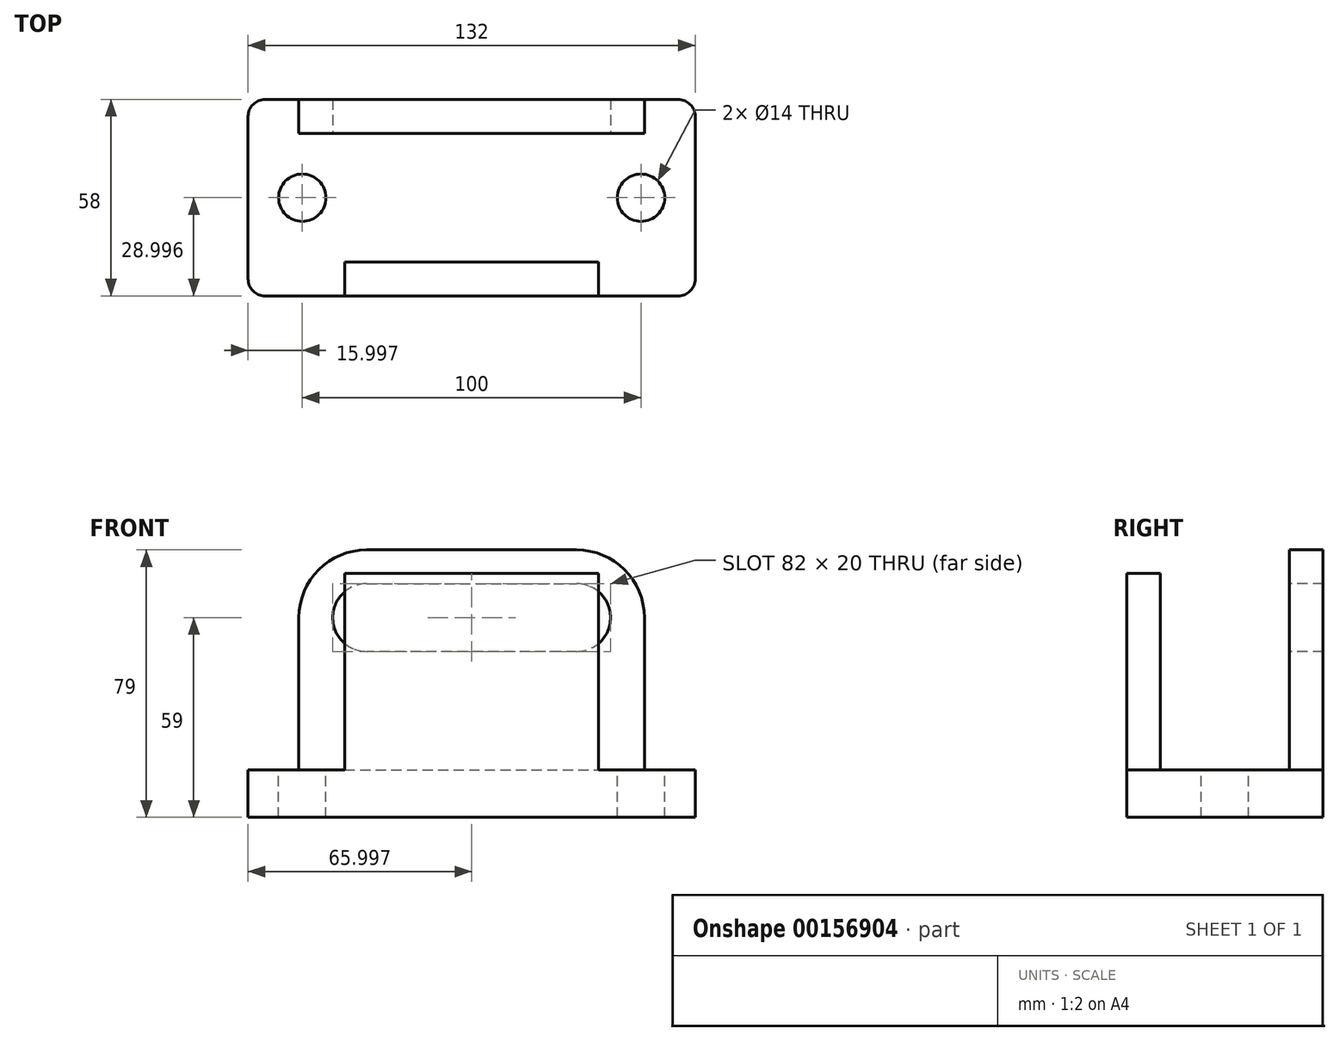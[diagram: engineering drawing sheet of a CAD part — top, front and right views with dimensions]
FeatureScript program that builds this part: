
annotation { "Feature Type Name" : "Feature", "Feature Type Description" : "" }
export const myFeature = defineFeature(function(context is Context, id is Id, definition is map)
    precondition{}
    {
        {
            var Q0;
            Q0=qCreatedBy(makeId("Top.planeOp"),FACE);
            var sketch = newSketch(context, id + "F0", { "sketchPlane" : qUnion([Q0])});
            skLineSegment(sketch, "E0.bottom", {"start": v(-73.57, -37.7) * mm, "end": v(48.43, -37.7) * mm});
            skLineSegment(sketch, "E0.top", {"start": v(-73.57, 20.3) * mm, "end": v(48.43, 20.3) * mm});
            skLineSegment(sketch, "E0.left", {"start": v(-78.57, -32.7) * mm, "end": v(-78.57, 15.3) * mm});
            skLineSegment(sketch, "E0.right", {"start": v(53.43, -32.7) * mm, "end": v(53.43, 15.3) * mm});
            skPoint(sketch, "E1.visualSharp", {"position": v(-78.57, -37.7) * mm});
            skArc(sketch, "E1.filletArc", {"start": v(-78.57, -32.7) * mm, "mid": v(-77.1, -36.24) * mm, "end": v(-73.57, -37.7) * mm});
            skPoint(sketch, "E2.visualSharp", {"position": v(53.43, -37.7) * mm});
            skArc(sketch, "E2.filletArc", {"start": v(48.43, -37.7) * mm, "mid": v(51.96, -36.24) * mm, "end": v(53.43, -32.7) * mm});
            skPoint(sketch, "E3.visualSharp", {"position": v(53.43, 20.3) * mm});
            skArc(sketch, "E3.filletArc", {"start": v(53.43, 15.3) * mm, "mid": v(51.96, 18.83) * mm, "end": v(48.43, 20.3) * mm});
            skPoint(sketch, "E4.visualSharp", {"position": v(-78.57, 20.3) * mm});
            skArc(sketch, "E4.filletArc", {"start": v(-73.57, 20.3) * mm, "mid": v(-77.1, 18.83) * mm, "end": v(-78.57, 15.3) * mm});
            skSolve(sketch);
        }
        {
            var Q0;
            Q0=makeQuery(id+"F0.imprint","IMPRINT",FACE,{"disambiguationData":[TD([[makeQuery(id+"F0.imprint","IMPRINT",EDGE,{"derivedFrom":sQuery(id+"F0.wireOp",EDGE,"E0.bottom")}),1.0]])]});
            extrude(context, id + "F1", {"entities" : qUnion([Q0]), "depth" : 14 * mm});
        }
        {
            var Q0;
            Q0=makeQuery(id+"F1.opExtrude","CAP_FACE",FACE,{"disambiguationData":[OSD([sQuery(id+"F0.wireOp",EDGE,"E0.bottom"),sQuery(id+"F0.wireOp",EDGE,"E0.top"),sQuery(id+"F0.wireOp",EDGE,"E0.left"),sQuery(id+"F0.wireOp",EDGE,"E0.right"),sQuery(id+"F0.wireOp",EDGE,"E1.filletArc"),sQuery(id+"F0.wireOp",EDGE,"E2.filletArc"),sQuery(id+"F0.wireOp",EDGE,"E3.filletArc"),sQuery(id+"F0.wireOp",EDGE,"E4.filletArc")])],"isStart":false});
            var sketch = newSketch(context, id + "F2", { "sketchPlane" : qUnion([Q0])});
            skLineSegment(sketch, "E5", {"start": v(-78.57, 15.3) * mm, "end": v(-78.57, 20.3) * mm});
            skLineSegment(sketch, "E6", {"start": v(-78.57, 20.3) * mm, "end": v(-63.57, 20.3) * mm});
            skLineSegment(sketch, "E7", {"start": v(-63.57, 20.3) * mm, "end": v(-63.57, 10.3) * mm});
            skLineSegment(sketch, "E8", {"start": v(-63.57, 10.3) * mm, "end": v(38.43, 10.3) * mm});
            skLineSegment(sketch, "E9", {"start": v(38.43, 10.3) * mm, "end": v(38.43, 20.3) * mm});
            skLineSegment(sketch, "E10", {"start": v(38.43, 20.3) * mm, "end": v(-63.57, 20.3) * mm});
            skSolve(sketch);
        }
        {
            var Q0;
            Q0=makeQuery(id+"F2.imprint","IMPRINT",FACE,{"disambiguationData":[TD([[makeQuery(id+"F2.imprint","IMPRINT",EDGE,{"derivedFrom":sQuery(id+"F2.wireOp",EDGE,"E7")}),1.0]])]});
            extrude(context, id + "F3", {"entities" : qUnion([Q0]), "operationType" : NewBodyOperationType.ADD, "depth" : 65 * mm});
        }
        {
            var Q0;
            Q0=makeQuery(id+"F3.opExtrude","CAP_EDGE",EDGE,{"disambiguationData":[OSD([sQuery(id+"F2.wireOp",EDGE,"E7")])],"isStart":false});
            var Q1;
            Q1=makeQuery(id+"F3.opExtrude","CAP_EDGE",EDGE,{"disambiguationData":[OSD([sQuery(id+"F2.wireOp",EDGE,"E9")])],"isStart":false});
            fillet(context, id + "F4", {"entities" : qUnion([Q0, Q1]), "radius" : 20 * mm, "tangentPropagation" : true, "allowEdgeOverflow" : false});
        }
        {
            var Q0;
            Q0=makeQuery(id+"F3.opExtrude","SWEPT_FACE",FACE,{"disambiguationData":[OSD([sQuery(id+"F2.wireOp",EDGE,"E8")])]});
            var sketch = newSketch(context, id + "F5", { "sketchPlane" : qUnion([Q0])});
            skLineSegment(sketch, "E11", {"start": v(-43.57, 69) * mm, "end": v(18.43, 69) * mm});
            skLineSegment(sketch, "E12", {"start": v(18.43, 49) * mm, "end": v(-43.57, 49) * mm});
            skArc(sketch, "E13", {"start": v(-43.57, 69) * mm, "mid": v(-53.57, 59) * mm, "end": v(-43.57, 49) * mm});
            skArc(sketch, "E14", {"start": v(18.43, 69) * mm, "mid": v(28.43, 59) * mm, "end": v(18.43, 49) * mm});
            skSolve(sketch);
        }
        {
            var Q0;
            Q0 = qSketchRegion(id + "F5", true);
            extrude(context, id + "F6", {"entities" : qUnion([Q0]), "operationType" : NewBodyOperationType.REMOVE, "oppositeDirection" : true, "depth" : 10 * mm});
        }
        {
            var Q0;
            Q0=makeQuery(id+"F1.opExtrude","CAP_FACE",FACE,{"disambiguationData":[OSD([sQuery(id+"F0.wireOp",EDGE,"E0.bottom"),sQuery(id+"F0.wireOp",EDGE,"E0.top"),sQuery(id+"F0.wireOp",EDGE,"E0.left"),sQuery(id+"F0.wireOp",EDGE,"E0.right"),sQuery(id+"F0.wireOp",EDGE,"E1.filletArc"),sQuery(id+"F0.wireOp",EDGE,"E2.filletArc"),sQuery(id+"F0.wireOp",EDGE,"E3.filletArc"),sQuery(id+"F0.wireOp",EDGE,"E4.filletArc")])],"isStart":false});
            var sketch = newSketch(context, id + "F7", { "sketchPlane" : qUnion([Q0])});
            skCircle(sketch, "E15", {"center": v(-62.57, -8.7) * mm, "radius": 7 * mm});
            skCircle(sketch, "E16", {"center": v(37.43, -8.7) * mm, "radius": 7 * mm});
            skSolve(sketch);
        }
        {
            var Q0;
            Q0=makeQuery(id+"F7.imprint","IMPRINT",FACE,{"disambiguationData":[TD([[makeQuery(id+"F7.imprint","IMPRINT",EDGE,{"derivedFrom":sQuery(id+"F7.wireOp",EDGE,"E15")}),1.0]])]});
            extrude(context, id + "F8", {"entities" : qUnion([Q0]), "operationType" : NewBodyOperationType.REMOVE, "oppositeDirection" : true, "depth" : 14 * mm});
        }
        {
            var Q0;
            Q0=makeQuery(id+"F1.opExtrude","CAP_FACE",FACE,{"disambiguationData":[OSD([sQuery(id+"F0.wireOp",EDGE,"E0.bottom"),sQuery(id+"F0.wireOp",EDGE,"E0.top"),sQuery(id+"F0.wireOp",EDGE,"E0.left"),sQuery(id+"F0.wireOp",EDGE,"E0.right"),sQuery(id+"F0.wireOp",EDGE,"E1.filletArc"),sQuery(id+"F0.wireOp",EDGE,"E2.filletArc"),sQuery(id+"F0.wireOp",EDGE,"E3.filletArc"),sQuery(id+"F0.wireOp",EDGE,"E4.filletArc")])],"isStart":false});
            var sketch = newSketch(context, id + "F9", { "sketchPlane" : qUnion([Q0])});
            skCircle(sketch, "E17", {"center": v(37.43, -8.7) * mm, "radius": 7 * mm});
            skSolve(sketch);
        }
        {
            var Q0;
            Q0=makeQuery(id+"F9.imprint","IMPRINT",FACE,{"disambiguationData":[TD([[makeQuery(id+"F9.imprint","IMPRINT",EDGE,{"derivedFrom":sQuery(id+"F9.wireOp",EDGE,"E17")}),1.0]])]});
            extrude(context, id + "F10", {"entities" : qUnion([Q0]), "operationType" : NewBodyOperationType.REMOVE, "oppositeDirection" : true, "depth" : 14 * mm});
        }
        {
            var Q0;
            Q0=makeQuery(id+"F1.opExtrude","CAP_FACE",FACE,{"disambiguationData":[OSD([sQuery(id+"F0.wireOp",EDGE,"E0.bottom"),sQuery(id+"F0.wireOp",EDGE,"E0.top"),sQuery(id+"F0.wireOp",EDGE,"E0.left"),sQuery(id+"F0.wireOp",EDGE,"E0.right"),sQuery(id+"F0.wireOp",EDGE,"E1.filletArc"),sQuery(id+"F0.wireOp",EDGE,"E2.filletArc"),sQuery(id+"F0.wireOp",EDGE,"E3.filletArc"),sQuery(id+"F0.wireOp",EDGE,"E4.filletArc")])],"isStart":false});
            var sketch = newSketch(context, id + "F11", { "sketchPlane" : qUnion([Q0])});
            skLineSegment(sketch, "E18", {"start": v(-12.57, -37.7) * mm, "end": v(-50.07, -37.7) * mm});
            skLineSegment(sketch, "E19", {"start": v(-50.07, -37.7) * mm, "end": v(-50.07, -27.7) * mm});
            skLineSegment(sketch, "E20", {"start": v(-50.07, -27.7) * mm, "end": v(24.93, -27.7) * mm});
            skLineSegment(sketch, "E21", {"start": v(24.93, -27.7) * mm, "end": v(24.93, -37.7) * mm});
            skLineSegment(sketch, "E22", {"start": v(24.93, -37.7) * mm, "end": v(-12.57, -37.7) * mm});
            skSolve(sketch);
        }
        {
            var Q0;
            Q0=makeQuery(id+"F11.imprint","IMPRINT",FACE,{"disambiguationData":[TD([[makeQuery(id+"F11.imprint","IMPRINT",EDGE,{"derivedFrom":sQuery(id+"F11.wireOp",EDGE,"E18")}),1.0]])]});
            extrude(context, id + "F12", {"entities" : qUnion([Q0]), "operationType" : NewBodyOperationType.ADD, "depth" : 58 * mm});
        }
    });
